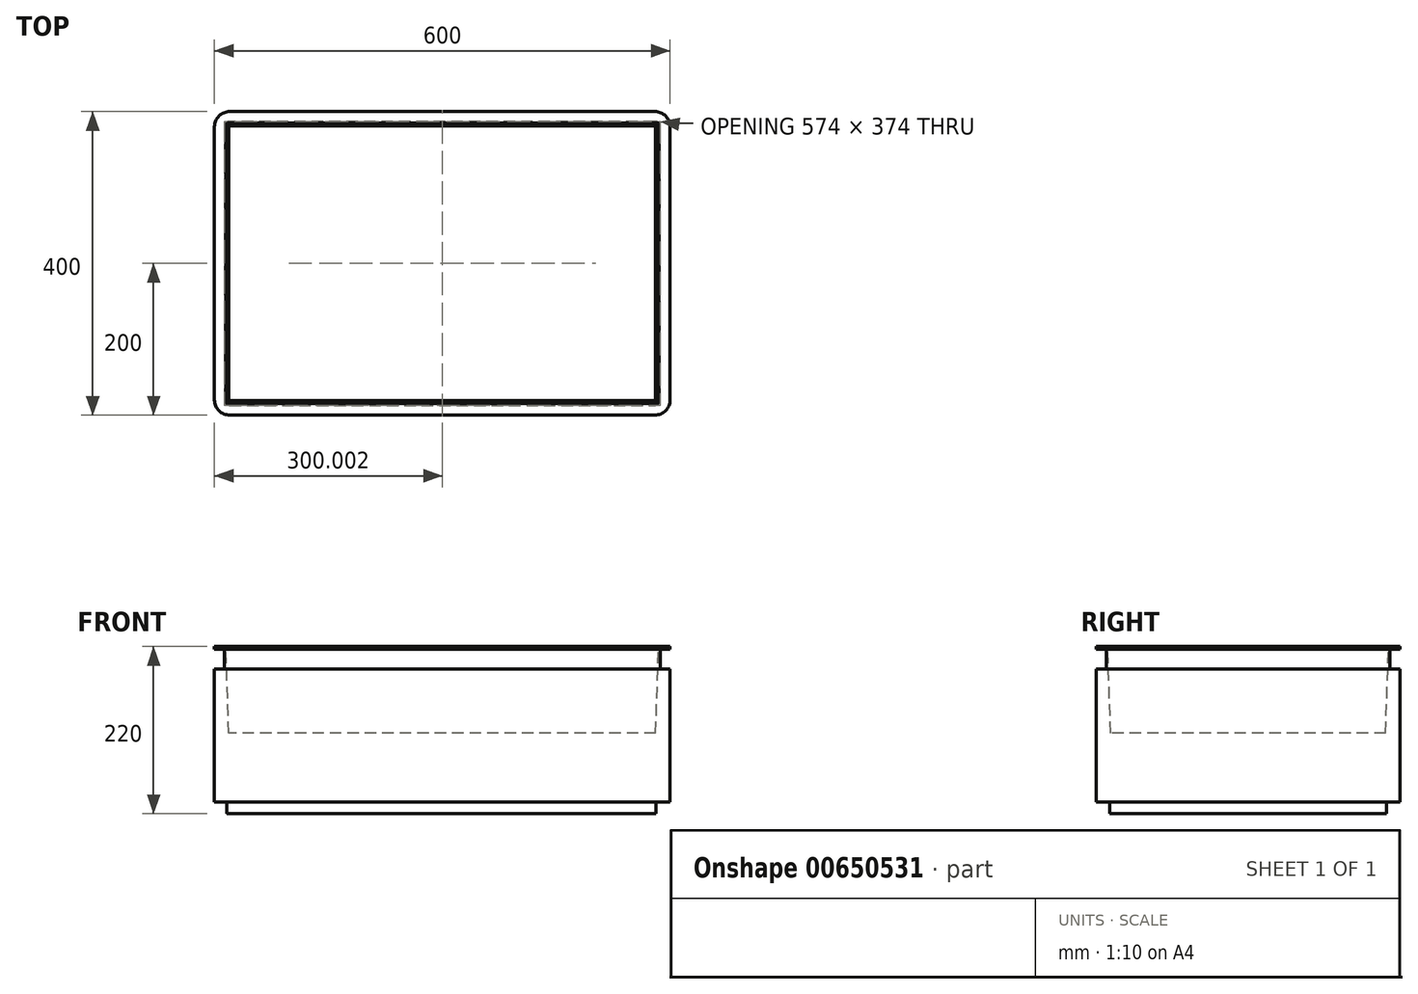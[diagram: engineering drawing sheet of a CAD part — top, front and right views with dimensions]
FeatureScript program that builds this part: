
annotation { "Feature Type Name" : "Feature", "Feature Type Description" : "" }
export const myFeature = defineFeature(function(context is Context, id is Id, definition is map)
    precondition{}
    {
        {
            var Q0;
            Q0=qCreatedBy(makeId("Top.planeOp"),FACE);
            var sketch = newSketch(context, id + "F0", { "sketchPlane" : qUnion([Q0])});
            skLineSegment(sketch, "E0.bottom", {"start": v(-291.39, 200) * mm, "end": v(308.61, 200) * mm});
            skLineSegment(sketch, "E0.top", {"start": v(-291.39, -200) * mm, "end": v(308.61, -200) * mm});
            skLineSegment(sketch, "E0.left", {"start": v(-291.39, 200) * mm, "end": v(-291.39, -200) * mm});
            skLineSegment(sketch, "E0.right", {"start": v(308.61, 200) * mm, "end": v(308.61, -200) * mm});
            skPoint(sketch, "E0.middle", {"position": v(8.61, 0) * mm});
            skSolve(sketch);
        }
        {
            var Q0;
            Q0=makeQuery(id+"F0.imprint","IMPRINT",FACE,{"disambiguationData":[TD([[makeQuery(id+"F0.imprint","IMPRINT",EDGE,{"derivedFrom":sQuery(id+"F0.wireOp",EDGE,"E0.bottom")}),-1.0]])]});
            extrude(context, id + "F1", {"entities" : qUnion([Q0]), "depth" : 220 * mm, "offsetDistance" : 25 * mm});
        }
        {
            var Q0;
            Q0=makeQuery(id+"F1.opExtrude","SWEPT_EDGE",EDGE,{"disambiguationData":[OSD([sQuery(id+"F0.wireOp",EDGE,"E0.top"),sQuery(id+"F0.wireOp",EDGE,"E0.left")])]});
            var Q1;
            Q1=makeQuery(id+"F1.opExtrude","SWEPT_EDGE",EDGE,{"disambiguationData":[OSD([sQuery(id+"F0.wireOp",EDGE,"E0.top"),sQuery(id+"F0.wireOp",EDGE,"E0.right")])]});
            var Q2;
            Q2=makeQuery(id+"F1.opExtrude","SWEPT_EDGE",EDGE,{"disambiguationData":[OSD([sQuery(id+"F0.wireOp",EDGE,"E0.bottom"),sQuery(id+"F0.wireOp",EDGE,"E0.right")])]});
            var Q3;
            Q3=makeQuery(id+"F1.opExtrude","SWEPT_EDGE",EDGE,{"disambiguationData":[OSD([sQuery(id+"F0.wireOp",EDGE,"E0.bottom"),sQuery(id+"F0.wireOp",EDGE,"E0.left")])]});
            fillet(context, id + "F2", {"entities" : qUnion([Q0, Q1, Q2, Q3]), "radius" : 20 * mm, "tangentPropagation" : true, "allowEdgeOverflow" : false});
        }
        {
            var Q0;
            Q0=makeQuery(id+"F1.opExtrude","CAP_FACE",FACE,{"disambiguationData":[OSD([sQuery(id+"F0.wireOp",EDGE,"E0.bottom"),sQuery(id+"F0.wireOp",EDGE,"E0.top"),sQuery(id+"F0.wireOp",EDGE,"E0.left"),sQuery(id+"F0.wireOp",EDGE,"E0.right")])],"isStart":true});
            var sketch = newSketch(context, id + "F3", { "sketchPlane" : qUnion([Q0])});
            skLineSegment(sketch, "E1.bottom", {"start": v(-270.1, 182.5) * mm, "end": v(284.9, 182.5) * mm});
            skLineSegment(sketch, "E1.top", {"start": v(-270.1, -182.5) * mm, "end": v(284.9, -182.5) * mm});
            skLineSegment(sketch, "E1.left", {"start": v(-275.1, 177.5) * mm, "end": v(-275.1, -177.5) * mm});
            skLineSegment(sketch, "E1.right", {"start": v(289.9, 177.5) * mm, "end": v(289.9, -177.5) * mm});
            skPoint(sketch, "E1.middle", {"position": v(7.4, 0) * mm});
            skLineSegment(sketch, "E2.0.0", {"start": v(288.61, 200) * mm, "end": v(-271.39, 200) * mm});
            skArc(sketch, "E2.0.1", {"start": v(-271.39, 200) * mm, "mid": v(-285.53, 194.14) * mm, "end": v(-291.39, 180) * mm});
            skLineSegment(sketch, "E2.0.2", {"start": v(-291.39, 180) * mm, "end": v(-291.39, -180) * mm});
            skArc(sketch, "E2.0.3", {"start": v(-291.39, -180) * mm, "mid": v(-285.53, -194.14) * mm, "end": v(-271.39, -200) * mm});
            skLineSegment(sketch, "E2.0.4", {"start": v(-271.39, -200) * mm, "end": v(288.61, -200) * mm});
            skArc(sketch, "E2.0.5", {"start": v(288.61, -200) * mm, "mid": v(302.75, -194.14) * mm, "end": v(308.61, -180) * mm});
            skLineSegment(sketch, "E2.0.6", {"start": v(308.61, -180) * mm, "end": v(308.61, 180) * mm});
            skArc(sketch, "E2.0.7", {"start": v(308.61, 180) * mm, "mid": v(302.75, 194.14) * mm, "end": v(288.61, 200) * mm});
            skPoint(sketch, "E3.visualSharp", {"position": v(-275.1, 182.5) * mm});
            skArc(sketch, "E3.filletArc", {"start": v(-270.1, 182.5) * mm, "mid": v(-273.63, 181.04) * mm, "end": v(-275.1, 177.5) * mm});
            skPoint(sketch, "E4.visualSharp", {"position": v(289.9, 182.5) * mm});
            skArc(sketch, "E4.filletArc", {"start": v(289.9, 177.5) * mm, "mid": v(288.44, 181.04) * mm, "end": v(284.9, 182.5) * mm});
            skPoint(sketch, "E5.visualSharp", {"position": v(289.9, -182.5) * mm});
            skArc(sketch, "E5.filletArc", {"start": v(284.9, -182.5) * mm, "mid": v(288.44, -181.04) * mm, "end": v(289.9, -177.5) * mm});
            skPoint(sketch, "E6.visualSharp", {"position": v(-275.1, -182.5) * mm});
            skArc(sketch, "E6.filletArc", {"start": v(-275.1, -177.5) * mm, "mid": v(-273.63, -181.04) * mm, "end": v(-270.1, -182.5) * mm});
            skSolve(sketch);
        }
        {
            var Q0;
            Q0=makeQuery(id+"F3.imprint","IMPRINT",FACE,{"disambiguationData":[TD([[makeQuery(id+"F3.imprint","IMPRINT",EDGE,{"derivedFrom":sQuery(id+"F3.wireOp",EDGE,"E1.bottom")}),1.0]])]});
            extrude(context, id + "F4", {"entities" : qUnion([Q0]), "operationType" : NewBodyOperationType.REMOVE, "oppositeDirection" : true, "depth" : 15 * mm, "offsetDistance" : 25 * mm});
        }
        {
            var Q0;
            Q0=makeQuery(id+"F1.opExtrude","CAP_FACE",FACE,{"disambiguationData":[OSD([sQuery(id+"F0.wireOp",EDGE,"E0.bottom"),sQuery(id+"F0.wireOp",EDGE,"E0.top"),sQuery(id+"F0.wireOp",EDGE,"E0.left"),sQuery(id+"F0.wireOp",EDGE,"E0.right")])],"isStart":false});
            cPlane(context, id + "F5", {"entities" : qUnion([Q0]), "cplaneType" : CPlaneType.OFFSET, "offset" : 3.5 * mm, "oppositeDirection" : true, "width" : 150 * mm, "height" : 150 * mm});
        }
        {
            var Q0;
            Q0=qCreatedBy(id+"F5.planeOp",FACE);
            var sketch = newSketch(context, id + "F6", { "sketchPlane" : qUnion([Q0])});
            skLineSegment(sketch, "E7.0.0", {"start": v(-291.39, 180) * mm, "end": v(-291.39, -180) * mm});
            skArc(sketch, "E7.0.1", {"start": v(-291.39, -180) * mm, "mid": v(-285.53, -194.14) * mm, "end": v(-271.39, -200) * mm});
            skLineSegment(sketch, "E7.0.2", {"start": v(-271.39, -200) * mm, "end": v(288.61, -200) * mm});
            skArc(sketch, "E7.0.3", {"start": v(288.61, -200) * mm, "mid": v(302.75, -194.14) * mm, "end": v(308.61, -180) * mm});
            skLineSegment(sketch, "E7.0.4", {"start": v(308.61, -180) * mm, "end": v(308.61, 180) * mm});
            skArc(sketch, "E7.0.5", {"start": v(308.61, 180) * mm, "mid": v(302.75, 194.14) * mm, "end": v(288.61, 200) * mm});
            skLineSegment(sketch, "E7.0.6", {"start": v(288.61, 200) * mm, "end": v(-271.39, 200) * mm});
            skArc(sketch, "E7.0.7", {"start": v(-271.39, 200) * mm, "mid": v(-285.53, 194.14) * mm, "end": v(-291.39, 180) * mm});
            skArc(sketch, "E8.0", {"start": v(-271.39, 187) * mm, "mid": v(-276.34, 184.95) * mm, "end": v(-278.39, 180) * mm});
            skLineSegment(sketch, "E8.1", {"start": v(288.61, 187) * mm, "end": v(-271.39, 187) * mm});
            skLineSegment(sketch, "E8.2", {"start": v(-278.39, 180) * mm, "end": v(-278.39, -180) * mm});
            skArc(sketch, "E8.3", {"start": v(295.61, 180) * mm, "mid": v(293.56, 184.95) * mm, "end": v(288.61, 187) * mm});
            skArc(sketch, "E8.4", {"start": v(-278.39, -180) * mm, "mid": v(-276.34, -184.95) * mm, "end": v(-271.39, -187) * mm});
            skLineSegment(sketch, "E8.5", {"start": v(-271.39, -187) * mm, "end": v(288.61, -187) * mm});
            skArc(sketch, "E8.6", {"start": v(288.61, -187) * mm, "mid": v(293.56, -184.95) * mm, "end": v(295.61, -180) * mm});
            skLineSegment(sketch, "E8.7", {"start": v(295.61, -180) * mm, "end": v(295.61, 180) * mm});
            skSolve(sketch);
        }
        {
            var Q0;
            Q0=qSketchRegion(id+"F6",true);
            extrude(context, id + "F7", {"entities" : qUnion([Q0]), "operationType" : NewBodyOperationType.REMOVE, "oppositeDirection" : true, "depth" : 26 * mm, "offsetDistance" : 25 * mm});
        }
        {
            var Q0;
            Q0=makeQuery(id+"F1.opExtrude","CAP_FACE",FACE,{"disambiguationData":[OSD([sQuery(id+"F0.wireOp",EDGE,"E0.bottom"),sQuery(id+"F0.wireOp",EDGE,"E0.top"),sQuery(id+"F0.wireOp",EDGE,"E0.left"),sQuery(id+"F0.wireOp",EDGE,"E0.right")])],"isStart":false});
            var sketch = newSketch(context, id + "F8", { "sketchPlane" : qUnion([Q0])});
            skLineSegment(sketch, "E9.0", {"start": v(-276.39, 185) * mm, "end": v(-276.39, -185) * mm});
            skLineSegment(sketch, "E9.1", {"start": v(293.61, 185) * mm, "end": v(-276.39, 185) * mm});
            skLineSegment(sketch, "E9.2", {"start": v(293.61, -185) * mm, "end": v(293.61, 185) * mm});
            skLineSegment(sketch, "E9.3", {"start": v(-276.39, -185) * mm, "end": v(293.61, -185) * mm});
            skSolve(sketch);
        }
        {
            var Q0;
            Q0=makeQuery(id+"F8.imprint","IMPRINT",FACE,{"disambiguationData":[TD([[makeQuery(id+"F8.imprint","IMPRINT",EDGE,{"derivedFrom":sQuery(id+"F8.wireOp",EDGE,"E9.0")}),1.0]])]});
            extrude(context, id + "F9", {"entities" : qUnion([Q0]), "operationType" : NewBodyOperationType.REMOVE, "oppositeDirection" : true, "depth" : 114 * mm, "offsetDistance" : 25 * mm, "hasDraft" : true, "draftAngle" : 2 * degree, "draftPullDirection" : true});
        }
    });
